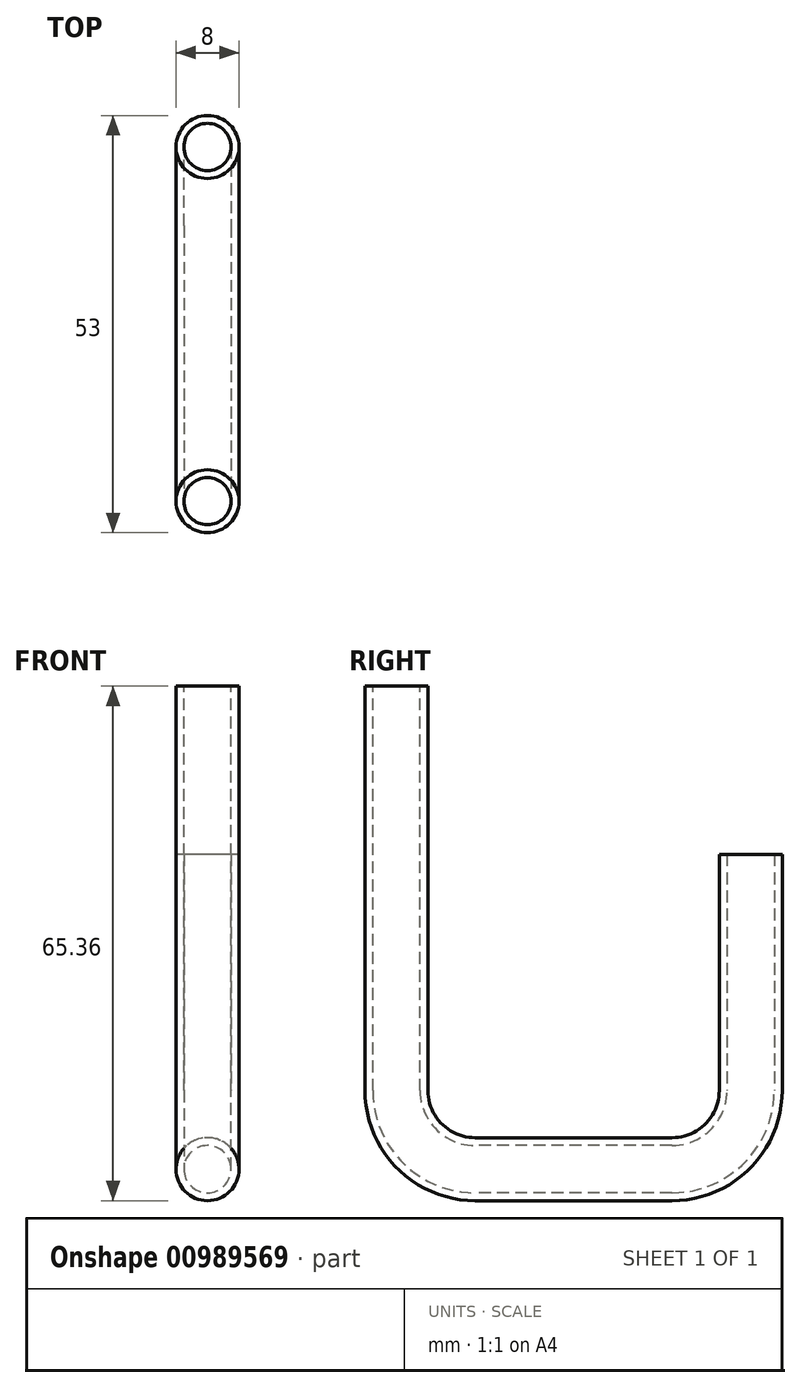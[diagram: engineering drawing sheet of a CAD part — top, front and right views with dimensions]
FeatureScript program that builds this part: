
annotation { "Feature Type Name" : "Feature", "Feature Type Description" : "" }
export const myFeature = defineFeature(function(context is Context, id is Id, definition is map)
    precondition{}
    {
        {
            var Q0;
            Q0=qCreatedBy(makeId("Top.planeOp"), FACE);
            var sketch = newSketch(context, id + "F0", { "sketchPlane" : qUnion([Q0])});
            skCircle(sketch, "E0", {"center": v(0, 0) * mm, "radius": 4 * mm});
            skCircle(sketch, "E1", {"center": v(0, 0) * mm, "radius": 3 * mm});
            skSolve(sketch);
        }
        {
            var Q0;
            Q0=qCreatedBy(makeId("Right.planeOp"), FACE);
            var sketch = newSketch(context, id + "F1", { "sketchPlane" : qUnion([Q0])});
            skLineSegment(sketch, "E2", {"start": v(0, 0) * mm, "end": v(0, -30) * mm});
            skLineSegment(sketch, "E3", {"start": v(-10, -40) * mm, "end": v(-35, -40) * mm});
            skLineSegment(sketch, "E4", {"start": v(-45, -30) * mm, "end": v(-45, -3.07) * mm});
            skPoint(sketch, "E5.visualSharp", {"position": v(0, -40) * mm});
            skArc(sketch, "E5.filletArc", {"start": v(-10, -40) * mm, "mid": v(-2.93, -37.07) * mm, "end": v(0, -30) * mm});
            skPoint(sketch, "E6.visualSharp", {"position": v(-45, -40) * mm});
            skArc(sketch, "E6.filletArc", {"start": v(-45, -30) * mm, "mid": v(-42.07, -37.07) * mm, "end": v(-35, -40) * mm});
            skLineSegment(sketch, "E7", {"start": v(-45, -3.07) * mm, "end": v(-45, 21.36) * mm});
            skSolve(sketch);
        }
        {
            var Q0;
            Q0 = qSketchRegion(id + "F0", true);
            var Q1;
            Q1 = qConstructionFilter(qBodyType(qCreatedBy(id + "F1" ,EDGE), BodyType.WIRE), ConstructionObject.NO);
            sweep(context, id + "F2", {"profiles" : qUnion([Q0]), "path" : qUnion([Q1])});
        }
    });
